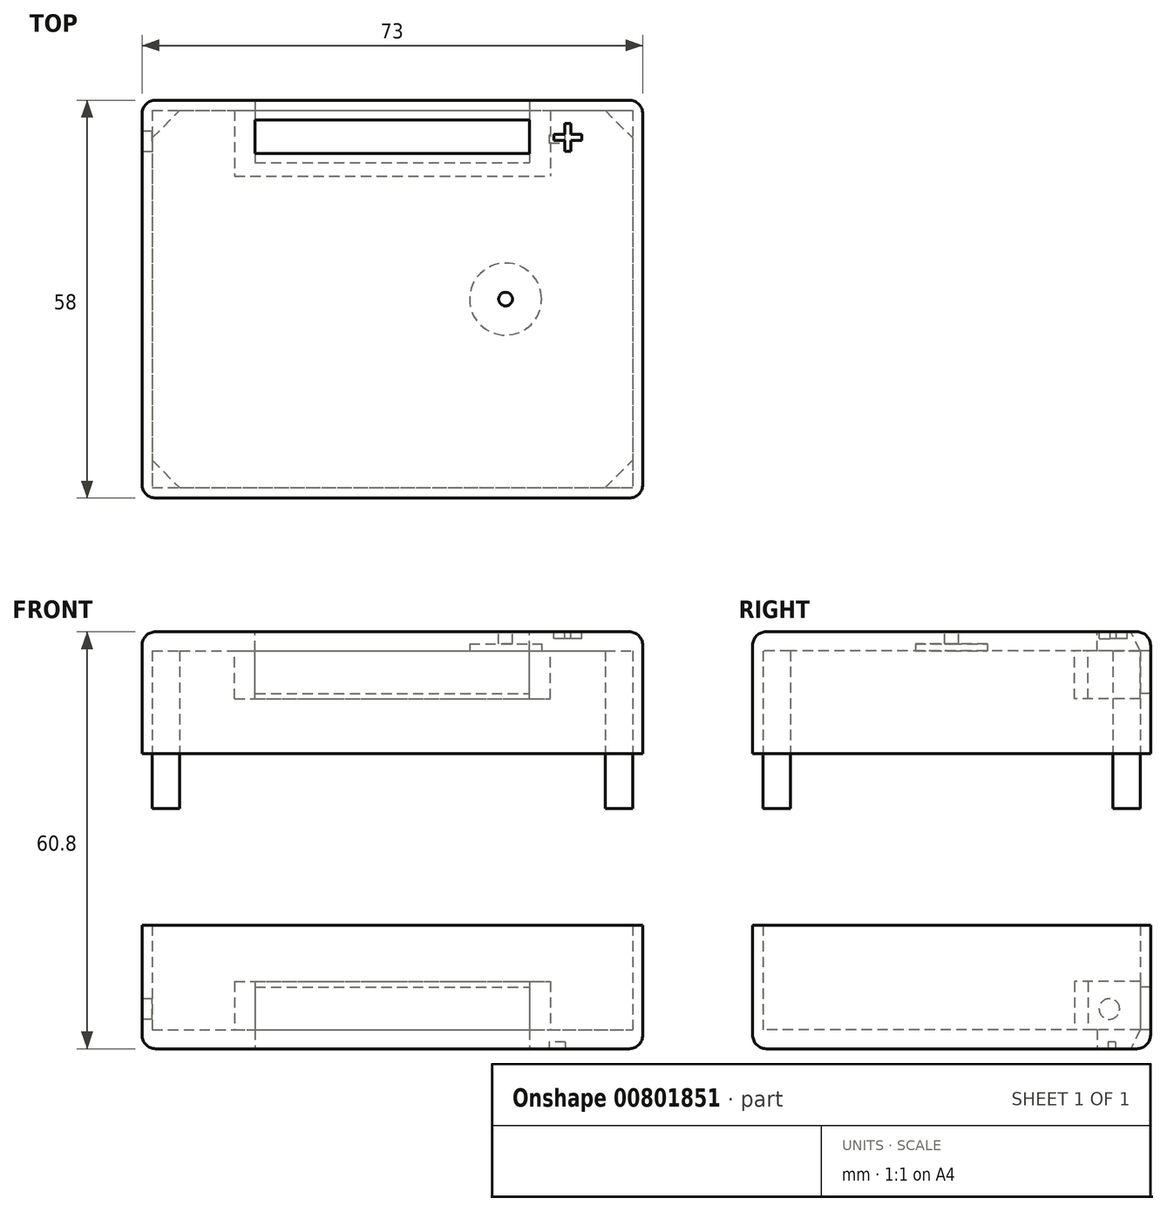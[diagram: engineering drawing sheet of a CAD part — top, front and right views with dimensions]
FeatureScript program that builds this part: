
annotation { "Feature Type Name" : "Feature", "Feature Type Description" : "" }
export const myFeature = defineFeature(function(context is Context, id is Id, definition is map)
    precondition{}
    {
        {
            var Q0;
            Q0=qCreatedBy(makeId("Top.planeOp"),FACE);
            var sketch = newSketch(context, id + "F0", { "sketchPlane" : qUnion([Q0])});
            skLineSegment(sketch, "E0.bottom", {"start": v(0, 55) * mm, "end": v(70, 55) * mm});
            skLineSegment(sketch, "E0.top", {"start": v(0, 0) * mm, "end": v(70, 0) * mm});
            skLineSegment(sketch, "E0.left", {"start": v(0, 55) * mm, "end": v(0, 0) * mm});
            skLineSegment(sketch, "E0.right", {"start": v(70, 55) * mm, "end": v(70, 0) * mm});
            skLineSegment(sketch, "E1.bottom", {"start": v(0.5, 56.5) * mm, "end": v(69.5, 56.5) * mm});
            skLineSegment(sketch, "E1.top", {"start": v(0.5, -1.5) * mm, "end": v(69.5, -1.5) * mm});
            skLineSegment(sketch, "E1.left", {"start": v(-1.5, 54.5) * mm, "end": v(-1.5, 0.5) * mm});
            skLineSegment(sketch, "E1.right", {"start": v(71.5, 54.5) * mm, "end": v(71.5, 0.5) * mm});
            skPoint(sketch, "E2.visualSharp", {"position": v(-1.5, 56.5) * mm});
            skArc(sketch, "E2.filletArc", {"start": v(0.5, 56.5) * mm, "mid": v(-0.91, 55.91) * mm, "end": v(-1.5, 54.5) * mm});
            skPoint(sketch, "E3.visualSharp", {"position": v(-1.5, -1.5) * mm});
            skArc(sketch, "E3.filletArc", {"start": v(-1.5, 0.5) * mm, "mid": v(-0.91, -0.91) * mm, "end": v(0.5, -1.5) * mm});
            skPoint(sketch, "E4.visualSharp", {"position": v(71.5, 56.5) * mm});
            skArc(sketch, "E4.filletArc", {"start": v(71.5, 54.5) * mm, "mid": v(70.91, 55.91) * mm, "end": v(69.5, 56.5) * mm});
            skPoint(sketch, "E5.visualSharp", {"position": v(71.5, -1.5) * mm});
            skArc(sketch, "E5.filletArc", {"start": v(69.5, -1.5) * mm, "mid": v(70.91, -0.91) * mm, "end": v(71.5, 0.5) * mm});
            skSolve(sketch);
        }
        {
            var Q0;
            Q0=makeQuery(id+"F0.imprint","IMPRINT",FACE,{"disambiguationData":[TD([[makeQuery(id+"F0.imprint","IMPRINT",EDGE,{"derivedFrom":sQuery(id+"F0.wireOp",EDGE,"E0.bottom")}),-1.0]])]});
            extrude(context, id + "F1", {"entities" : qUnion([Q0]), "depth" : 2.8 * mm, "offsetDistance" : 25 * mm});
        }
        {
            var Q0;
            Q0=makeQuery(id+"F0.imprint","IMPRINT",FACE,{"disambiguationData":[TD([[makeQuery(id+"F0.imprint","IMPRINT",EDGE,{"derivedFrom":sQuery(id+"F0.wireOp",EDGE,"E0.bottom")}),1.0]])]});
            extrude(context, id + "F2", {"entities" : qUnion([Q0]), "operationType" : NewBodyOperationType.ADD, "depth" : 18 * mm, "offsetDistance" : 25 * mm});
        }
        {
            var Q0;
            Q0=makeQuery(id+"F1.opExtrude","CAP_FACE",FACE,{"disambiguationData":[OSD([sQuery(id+"F0.wireOp",EDGE,"E0.bottom"),sQuery(id+"F0.wireOp",EDGE,"E0.top"),sQuery(id+"F0.wireOp",EDGE,"E0.left"),sQuery(id+"F0.wireOp",EDGE,"E0.right")])],"isStart":false});
            var sketch = newSketch(context, id + "F3", { "sketchPlane" : qUnion([Q0])});
            skLineSegment(sketch, "E6.bottom", {"start": v(12, 55) * mm, "end": v(15, 55) * mm});
            skLineSegment(sketch, "E6.right", {"start": v(15, 55) * mm, "end": v(15, 47.4) * mm});
            skLineSegment(sketch, "E7.bottom", {"start": v(55, 55) * mm, "end": v(58, 55) * mm});
            skLineSegment(sketch, "E7.left", {"start": v(55, 55) * mm, "end": v(55, 47.4) * mm});
            skLineSegment(sketch, "E8", {"start": v(12, 51.2) * mm, "end": v(0, 51.2) * mm, "construction": true});
            skLineSegment(sketch, "E9", {"start": v(58, 51.2) * mm, "end": v(70, 51.2) * mm, "construction": true});
            skLineSegment(sketch, "E10.bottom", {"start": v(15, 47.4) * mm, "end": v(55, 47.4) * mm});
            skLineSegment(sketch, "E10.top", {"start": v(12, 45.4) * mm, "end": v(58, 45.4) * mm});
            skLineSegment(sketch, "E11", {"start": v(12, 55) * mm, "end": v(12, 45.4) * mm});
            skLineSegment(sketch, "E12", {"start": v(58, 55) * mm, "end": v(58, 45.4) * mm});
            skLineSegment(sketch, "E13", {"start": v(15, 48.7) * mm, "end": v(55, 48.7) * mm});
            skLineSegment(sketch, "E14", {"start": v(15, 55) * mm, "end": v(55, 55) * mm});
            skSolve(sketch);
        }
        {
            var Q0;
            Q0=makeQuery(id+"F3.imprint","IMPRINT",FACE,{"disambiguationData":[TD([[makeQuery(id+"F3.imprint","IMPRINT",EDGE,{"derivedFrom":sQuery(id+"F3.wireOp",EDGE,"E6.bottom")}),-1.0]])]});
            var Q1;
            Q1=makeQuery(id+"F3.imprint","IMPRINT",FACE,{"disambiguationData":[TD([[makeQuery(id+"F3.imprint","IMPRINT",EDGE,{"derivedFrom":sQuery(id+"F3.wireOp",EDGE,"E7.bottom")}),-1.0]])]});
            extrude(context, id + "F4", {"entities" : qUnion([Q0, Q1]), "operationType" : NewBodyOperationType.ADD, "depth" : 7 * mm, "offsetDistance" : 25 * mm});
        }
        {
            var Q0;
            {var subQ0=sQuery(id+"F0.wireOp",EDGE,"E0.right");var subQ1=sQuery(id+"F0.wireOp",EDGE,"E0.left");var subQ2=sQuery(id+"F0.wireOp",EDGE,"E0.top");var subQ3=sQuery(id+"F0.wireOp",EDGE,"E0.bottom");Q0=makeQuery(id+"F2.boolean.opBoolean","MERGE",FACE,{"derivedFrom":[makeQuery(id+"F1.opExtrude","CAP_FACE",FACE,{"disambiguationData":[OSD([subQ3,subQ2,subQ1,subQ0])],"isStart":true}),makeQuery(id+"F2.opExtrude","CAP_FACE",FACE,{"disambiguationData":[OSD([subQ3,subQ2,subQ1,subQ0,sQuery(id+"F0.wireOp",EDGE,"E1.bottom"),sQuery(id+"F0.wireOp",EDGE,"E1.top"),sQuery(id+"F0.wireOp",EDGE,"E1.left"),sQuery(id+"F0.wireOp",EDGE,"E1.right"),sQuery(id+"F0.wireOp",EDGE,"E2.filletArc"),sQuery(id+"F0.wireOp",EDGE,"E3.filletArc"),sQuery(id+"F0.wireOp",EDGE,"E4.filletArc"),sQuery(id+"F0.wireOp",EDGE,"E5.filletArc")])],"isStart":true})]});}
            var sketch = newSketch(context, id + "F5", { "sketchPlane" : qUnion([Q0])});
            skLineSegment(sketch, "E15.0", {"start": v(15, -48.7) * mm, "end": v(55, -48.7) * mm});
            skLineSegment(sketch, "E15.1", {"start": v(15, -53.6) * mm, "end": v(15, -48.7) * mm});
            skLineSegment(sketch, "E15.2", {"start": v(55, -53.6) * mm, "end": v(55, -48.7) * mm});
            skLineSegment(sketch, "E16", {"start": v(15, -55) * mm, "end": v(55, -55) * mm, "construction": true});
            skLineSegment(sketch, "E17", {"start": v(15, -53.6) * mm, "end": v(55, -53.6) * mm});
            skSolve(sketch);
        }
        {
            var Q1;
            {var subQ2=sQuery(id+"F3.wireOp",EDGE,"E13");Q1=makeQuery(id+"F3.imprint","IMPRINT",FACE,{"disambiguationData":[TD([[makeQuery(id+"F3.imprint","IMPRINT",EDGE,{"derivedFrom":subQ2}),1.0]])]});}
            var Q2;
            Q2=makeQuery(id+"F5.imprint","IMPRINT",FACE,{"disambiguationData":[TD([[makeQuery(id+"F5.imprint","IMPRINT",EDGE,{"derivedFrom":sQuery(id+"F5.wireOp",EDGE,"E15.0")}),-1.0]])]});
            loft(context, id + "F6", {"operationType" : NewBodyOperationType.REMOVE, "sheetProfilesArray" : [{ "sheetProfileEntities" : qUnion([Q1]) }, { "sheetProfileEntities" : qUnion([Q2]) }]});
        }
        {
            var Q0;
            Q0=makeQuery(id+"F2.opExtrude","SWEPT_FACE",FACE,{"disambiguationData":[OSD([sQuery(id+"F0.wireOp",EDGE,"E0.bottom")])]});
            var sketch = newSketch(context, id + "F7", { "sketchPlane" : qUnion([Q0])});
            skLineSegment(sketch, "E18.bottom", {"start": v(15, 2.8) * mm, "end": v(55, 2.8) * mm});
            skLineSegment(sketch, "E18.top", {"start": v(15, 9) * mm, "end": v(55, 9) * mm});
            skLineSegment(sketch, "E18.left", {"start": v(15, 2.8) * mm, "end": v(15, 9) * mm});
            skLineSegment(sketch, "E18.right", {"start": v(55, 2.8) * mm, "end": v(55, 9) * mm});
            skSolve(sketch);
        }
        {
            var Q0;
            Q0=makeQuery(id+"F7.imprint","IMPRINT",FACE,{"disambiguationData":[TD([[makeQuery(id+"F7.imprint","IMPRINT",EDGE,{"derivedFrom":sQuery(id+"F7.wireOp",EDGE,"E18.bottom")}),1.0]])]});
            extrude(context, id + "F8", {"entities" : qUnion([Q0]), "operationType" : NewBodyOperationType.REMOVE, "endBound" : BoundingType.UP_TO_NEXT, "oppositeDirection" : true, "depth" : 25 * mm, "offsetDistance" : 25 * mm});
        }
        {
            var Q0;
            Q0=makeQuery(id+"F2.opExtrude","SWEPT_FACE",FACE,{"disambiguationData":[OSD([sQuery(id+"F0.wireOp",EDGE,"E1.left")])]});
            var sketch = newSketch(context, id + "F9", { "sketchPlane" : qUnion([Q0])});
            skCircle(sketch, "E19", {"center": v(-50.5, 5.8) * mm, "radius": 1.5 * mm});
            skLineSegment(sketch, "E20.0", {"start": v(-55, 2.8) * mm, "end": v(0, 2.8) * mm, "construction": true});
            skLineSegment(sketch, "E20.1", {"start": v(-55, 18) * mm, "end": v(-55, 2.8) * mm, "construction": true});
            skSolve(sketch);
        }
        {
            var Q0;
            Q0=makeQuery(id+"F9.imprint","IMPRINT",FACE,{"disambiguationData":[TD([[makeQuery(id+"F9.imprint","IMPRINT",EDGE,{"derivedFrom":sQuery(id+"F9.wireOp",EDGE,"E19")}),1.0]])]});
            extrude(context, id + "F10", {"entities" : qUnion([Q0]), "operationType" : NewBodyOperationType.REMOVE, "endBound" : BoundingType.UP_TO_NEXT, "oppositeDirection" : true, "depth" : 25 * mm, "offsetDistance" : 25 * mm});
        }
        {
            var Q0;
            Q0=makeQuery(id+"F2.opExtrude","CAP_EDGE",EDGE,{"disambiguationData":[OSD([sQuery(id+"F0.wireOp",EDGE,"E1.top")])],"isStart":true});
            fillet(context, id + "F11", {"entities" : qUnion([Q0]), "radius" : 2 * mm, "tangentPropagation" : true, "allowEdgeOverflow" : false});
        }
        {
            var Q0;
            {var subQ0=sQuery(id+"F0.wireOp",EDGE,"E0.right");var subQ1=sQuery(id+"F0.wireOp",EDGE,"E0.left");var subQ2=sQuery(id+"F0.wireOp",EDGE,"E0.top");var subQ3=sQuery(id+"F0.wireOp",EDGE,"E0.bottom");Q0=makeQuery(id+"F2.boolean.opBoolean","MERGE",FACE,{"derivedFrom":[makeQuery(id+"F1.opExtrude","CAP_FACE",FACE,{"disambiguationData":[OSD([subQ3,subQ2,subQ1,subQ0])],"isStart":true}),makeQuery(id+"F2.opExtrude","CAP_FACE",FACE,{"disambiguationData":[OSD([subQ3,subQ2,subQ1,subQ0,sQuery(id+"F0.wireOp",EDGE,"E1.bottom"),sQuery(id+"F0.wireOp",EDGE,"E1.top"),sQuery(id+"F0.wireOp",EDGE,"E1.left"),sQuery(id+"F0.wireOp",EDGE,"E1.right"),sQuery(id+"F0.wireOp",EDGE,"E2.filletArc"),sQuery(id+"F0.wireOp",EDGE,"E3.filletArc"),sQuery(id+"F0.wireOp",EDGE,"E4.filletArc"),sQuery(id+"F0.wireOp",EDGE,"E5.filletArc")])],"isStart":true})]});}
            var sketch = newSketch(context, id + "F12", { "sketchPlane" : qUnion([Q0])});
            skText(sketch, "E21", { "text": "-", "fontName": "OpenSans-Bold.ttf"});
            const initialGuessF12  = {"E21": [0.0576, -0.05323, 1, 0, 0.00644]};
            skSetInitialGuess(sketch, initialGuessF12);
            skSolve(sketch);
        }
        {
            var Q0;
            Q0=makeQuery(id+"F12.imprint","IMPRINT",FACE,{"disambiguationData":[TD([[makeQuery(id+"F12.imprint","IMPRINT",EDGE,{"derivedFrom":sQuery(id+"F12.wireOp",EDGE,"E21.sketch_text.stroke-0")}),-1.0]])]});
            extrude(context, id + "F13", {"entities" : qUnion([Q0]), "operationType" : NewBodyOperationType.REMOVE, "oppositeDirection" : true, "depth" : 1 * mm, "offsetDistance" : 25 * mm});
        }
        {
            var Q0;
            Q0=makeQuery(id+"F2.opExtrude","CAP_FACE",FACE,{"disambiguationData":[OSD([sQuery(id+"F0.wireOp",EDGE,"E0.bottom"),sQuery(id+"F0.wireOp",EDGE,"E0.top"),sQuery(id+"F0.wireOp",EDGE,"E0.left"),sQuery(id+"F0.wireOp",EDGE,"E0.right"),sQuery(id+"F0.wireOp",EDGE,"E1.bottom"),sQuery(id+"F0.wireOp",EDGE,"E1.top"),sQuery(id+"F0.wireOp",EDGE,"E1.left"),sQuery(id+"F0.wireOp",EDGE,"E1.right"),sQuery(id+"F0.wireOp",EDGE,"E2.filletArc"),sQuery(id+"F0.wireOp",EDGE,"E3.filletArc"),sQuery(id+"F0.wireOp",EDGE,"E4.filletArc"),sQuery(id+"F0.wireOp",EDGE,"E5.filletArc")])],"isStart":false});
            cPlane(context, id + "F14", {"entities" : qUnion([Q0]), "cplaneType" : CPlaneType.OFFSET, "offset" : 25 * mm, "width" : 150 * mm, "height" : 150 * mm});
        }
        {
            var Q0;
            Q0=qCreatedBy(id+"F14.planeOp",FACE);
            var sketch = newSketch(context, id + "F15", { "sketchPlane" : qUnion([Q0])});
            skLineSegment(sketch, "E22.0", {"start": v(0, 55) * mm, "end": v(70, 55) * mm});
            skLineSegment(sketch, "E22.1", {"start": v(0, 55) * mm, "end": v(0, 0) * mm});
            skLineSegment(sketch, "E22.2", {"start": v(0, 0) * mm, "end": v(70, 0) * mm});
            skLineSegment(sketch, "E22.3", {"start": v(70, 55) * mm, "end": v(70, 0) * mm});
            skLineSegment(sketch, "E22.4", {"start": v(0.5, 56.5) * mm, "end": v(69.5, 56.5) * mm});
            skArc(sketch, "E22.5", {"start": v(0.5, 56.5) * mm, "mid": v(-0.91, 55.91) * mm, "end": v(-1.5, 54.5) * mm});
            skLineSegment(sketch, "E22.6", {"start": v(-1.5, 54.5) * mm, "end": v(-1.5, 0.5) * mm});
            skArc(sketch, "E22.7", {"start": v(-1.5, 0.5) * mm, "mid": v(-0.91, -0.91) * mm, "end": v(0.5, -1.5) * mm});
            skLineSegment(sketch, "E22.8", {"start": v(0.5, -1.5) * mm, "end": v(69.5, -1.5) * mm});
            skArc(sketch, "E22.9", {"start": v(69.5, -1.5) * mm, "mid": v(70.91, -0.91) * mm, "end": v(71.5, 0.5) * mm});
            skLineSegment(sketch, "E22.10", {"start": v(71.5, 54.5) * mm, "end": v(71.5, 0.5) * mm});
            skArc(sketch, "E22.11", {"start": v(71.5, 54.5) * mm, "mid": v(70.91, 55.91) * mm, "end": v(69.5, 56.5) * mm});
            skLineSegment(sketch, "E23", {"start": v(0, 51) * mm, "end": v(4, 55) * mm});
            skLineSegment(sketch, "E24", {"start": v(66, 55) * mm, "end": v(70, 51) * mm});
            skLineSegment(sketch, "E25", {"start": v(66, 0) * mm, "end": v(70, 4) * mm});
            skLineSegment(sketch, "E26", {"start": v(0, 4) * mm, "end": v(4, 0) * mm});
            skSolve(sketch);
        }
        {
            var Q0;
            Q0=makeQuery(id+"F15.imprint","IMPRINT",FACE,{"disambiguationData":[TD([[makeQuery(id+"F15.imprint","IMPRINT",EDGE,{"derivedFrom":sQuery(id+"F15.wireOp",EDGE,"E22.4")}),-1.0]])]});
            var Q1;
            {var subQ3=sQuery(id+"F15.wireOp",EDGE,"E26");Q1=makeQuery(id+"F15.imprint","IMPRINT",FACE,{"disambiguationData":[TD([[makeQuery(id+"F15.imprint","IMPRINT",EDGE,{"derivedFrom":subQ3}),-1.0]])]});}
            var Q2;
            {var subQ3=sQuery(id+"F15.wireOp",EDGE,"E23");Q2=makeQuery(id+"F15.imprint","IMPRINT",FACE,{"disambiguationData":[TD([[makeQuery(id+"F15.imprint","IMPRINT",EDGE,{"derivedFrom":subQ3}),1.0]])]});}
            var Q3;
            {var subQ3=sQuery(id+"F15.wireOp",EDGE,"E24");Q3=makeQuery(id+"F15.imprint","IMPRINT",FACE,{"disambiguationData":[TD([[makeQuery(id+"F15.imprint","IMPRINT",EDGE,{"derivedFrom":subQ3}),1.0]])]});}
            var Q4;
            {var subQ3=sQuery(id+"F15.wireOp",EDGE,"E25");Q4=makeQuery(id+"F15.imprint","IMPRINT",FACE,{"disambiguationData":[TD([[makeQuery(id+"F15.imprint","IMPRINT",EDGE,{"derivedFrom":subQ3}),-1.0]])]});}
            extrude(context, id + "F16", {"entities" : qUnion([Q0, Q1, Q2, Q3, Q4]), "depth" : 15 * mm, "offsetDistance" : 25 * mm});
        }
        {
            var Q0;
            Q0=makeQuery(id+"F16.opExtrude","CAP_FACE",FACE,{"disambiguationData":[OSD([sQuery(id+"F15.wireOp",EDGE,"E22.0"),sQuery(id+"F15.wireOp",EDGE,"E22.1"),sQuery(id+"F15.wireOp",EDGE,"E22.2"),sQuery(id+"F15.wireOp",EDGE,"E22.3"),sQuery(id+"F15.wireOp",EDGE,"E22.4"),sQuery(id+"F15.wireOp",EDGE,"E22.5"),sQuery(id+"F15.wireOp",EDGE,"E22.6"),sQuery(id+"F15.wireOp",EDGE,"E22.7"),sQuery(id+"F15.wireOp",EDGE,"E22.8"),sQuery(id+"F15.wireOp",EDGE,"E22.9"),sQuery(id+"F15.wireOp",EDGE,"E22.10"),sQuery(id+"F15.wireOp",EDGE,"E22.11")])],"isStart":false});
            var sketch = newSketch(context, id + "F17", { "sketchPlane" : qUnion([Q0])});
            skArc(sketch, "E27.0", {"start": v(0.5, 56.5) * mm, "mid": v(-0.91, 55.91) * mm, "end": v(-1.5, 54.5) * mm});
            skLineSegment(sketch, "E27.1", {"start": v(-1.5, 54.5) * mm, "end": v(-1.5, 0.5) * mm});
            skArc(sketch, "E27.2", {"start": v(-1.5, 0.5) * mm, "mid": v(-0.91, -0.91) * mm, "end": v(0.5, -1.5) * mm});
            skLineSegment(sketch, "E27.3", {"start": v(0.5, -1.5) * mm, "end": v(69.5, -1.5) * mm});
            skArc(sketch, "E27.4", {"start": v(69.5, -1.5) * mm, "mid": v(70.91, -0.91) * mm, "end": v(71.5, 0.5) * mm});
            skLineSegment(sketch, "E27.5", {"start": v(71.5, 54.5) * mm, "end": v(71.5, 0.5) * mm});
            skArc(sketch, "E27.6", {"start": v(71.5, 54.5) * mm, "mid": v(70.91, 55.91) * mm, "end": v(69.5, 56.5) * mm});
            skLineSegment(sketch, "E27.7", {"start": v(0.5, 56.5) * mm, "end": v(69.5, 56.5) * mm});
            skSolve(sketch);
        }
        {
            var Q0;
            Q0=makeQuery(id+"F17.imprint","IMPRINT",FACE,{"disambiguationData":[TD([[makeQuery(id+"F17.imprint","IMPRINT",EDGE,{"derivedFrom":makeQuery(id+"F16.opExtrude","CAP_EDGE",EDGE,{"disambiguationData":[OSD([sQuery(id+"F15.wireOp",EDGE,"E22.0")])],"isStart":false})}),-1.0]])]});
            var Q1;
            Q1=makeQuery(id+"F17.imprint","IMPRINT",FACE,{"disambiguationData":[TD([[makeQuery(id+"F17.imprint","IMPRINT",EDGE,{"derivedFrom":sQuery(id+"F17.wireOp",EDGE,"E27.0")}),1.0]])]});
            extrude(context, id + "F18", {"entities" : qUnion([Q0, Q1]), "operationType" : NewBodyOperationType.ADD, "depth" : 2.8 * mm, "offsetDistance" : 25 * mm});
        }
        {
            var Q0;
            Q0=makeQuery(id+"F18.opExtrude","CAP_FACE",FACE,{"disambiguationData":[OSD([sQuery(id+"F17.wireOp",EDGE,"E27.0"),sQuery(id+"F17.wireOp",EDGE,"E27.1"),sQuery(id+"F17.wireOp",EDGE,"E27.2"),sQuery(id+"F17.wireOp",EDGE,"E27.3"),sQuery(id+"F17.wireOp",EDGE,"E27.4"),sQuery(id+"F17.wireOp",EDGE,"E27.5"),sQuery(id+"F17.wireOp",EDGE,"E27.6"),sQuery(id+"F17.wireOp",EDGE,"E27.7")])],"isStart":true});
            var sketch = newSketch(context, id + "F19", { "sketchPlane" : qUnion([Q0])});
            skLineSegment(sketch, "E28.0", {"start": v(12, -55) * mm, "end": v(15, -55) * mm});
            skLineSegment(sketch, "E28.1", {"start": v(15, -55) * mm, "end": v(15, -47.4) * mm});
            skLineSegment(sketch, "E28.2", {"start": v(55, -55) * mm, "end": v(58, -55) * mm});
            skLineSegment(sketch, "E28.3", {"start": v(55, -55) * mm, "end": v(55, -47.4) * mm});
            skLineSegment(sketch, "E28.4", {"start": v(12, -51.2) * mm, "end": v(0, -51.2) * mm, "construction": true});
            skLineSegment(sketch, "E28.5", {"start": v(58, -51.2) * mm, "end": v(70, -51.2) * mm, "construction": true});
            skLineSegment(sketch, "E28.6", {"start": v(15, -47.4) * mm, "end": v(55, -47.4) * mm});
            skLineSegment(sketch, "E28.7", {"start": v(12, -45.4) * mm, "end": v(58, -45.4) * mm});
            skLineSegment(sketch, "E28.8", {"start": v(12, -55) * mm, "end": v(12, -45.4) * mm});
            skLineSegment(sketch, "E28.9", {"start": v(58, -55) * mm, "end": v(58, -45.4) * mm});
            skLineSegment(sketch, "E28.10", {"start": v(15, -48.7) * mm, "end": v(55, -48.7) * mm});
            skLineSegment(sketch, "E28.11", {"start": v(15, -55) * mm, "end": v(55, -55) * mm});
            skSolve(sketch);
        }
        {
            var Q0;
            Q0=makeQuery(id+"F18.opExtrude","CAP_FACE",FACE,{"disambiguationData":[OSD([sQuery(id+"F17.wireOp",EDGE,"E27.0"),sQuery(id+"F17.wireOp",EDGE,"E27.1"),sQuery(id+"F17.wireOp",EDGE,"E27.2"),sQuery(id+"F17.wireOp",EDGE,"E27.3"),sQuery(id+"F17.wireOp",EDGE,"E27.4"),sQuery(id+"F17.wireOp",EDGE,"E27.5"),sQuery(id+"F17.wireOp",EDGE,"E27.6"),sQuery(id+"F17.wireOp",EDGE,"E27.7")])],"isStart":false});
            var sketch = newSketch(context, id + "F20", { "sketchPlane" : qUnion([Q0])});
            skLineSegment(sketch, "E29.0.0", {"start": v(15, 48.7) * mm, "end": v(15, 53.6) * mm});
            skLineSegment(sketch, "E29.0.1", {"start": v(15, 53.6) * mm, "end": v(55, 53.6) * mm});
            skLineSegment(sketch, "E29.0.2", {"start": v(55, 53.6) * mm, "end": v(55, 48.7) * mm});
            skLineSegment(sketch, "E29.0.3", {"start": v(55, 48.7) * mm, "end": v(15, 48.7) * mm});
            skSolve(sketch);
        }
        {
            var Q1;
            {var subQ2=sQuery(id+"F19.wireOp",EDGE,"E28.10");Q1=makeQuery(id+"F19.imprint","IMPRINT",FACE,{"disambiguationData":[TD([[makeQuery(id+"F19.imprint","IMPRINT",EDGE,{"derivedFrom":subQ2}),-1.0]])]});}
            var Q2;
            Q2=makeQuery(id+"F20.imprint","IMPRINT",FACE,{"disambiguationData":[TD([[makeQuery(id+"F20.imprint","IMPRINT",EDGE,{"derivedFrom":sQuery(id+"F20.wireOp",EDGE,"E29.0.0")}),-1.0]])]});
            loft(context, id + "F21", {"operationType" : NewBodyOperationType.REMOVE, "sheetProfilesArray" : [{ "sheetProfileEntities" : qUnion([Q1]) }, { "sheetProfileEntities" : qUnion([Q2]) }]});
        }
        {
            var Q0;
            {var subQ6=sQuery(id+"F19.wireOp",EDGE,"E28.0");Q0=makeQuery(id+"F19.imprint","IMPRINT",FACE,{"disambiguationData":[TD([[makeQuery(id+"F19.imprint","IMPRINT",EDGE,{"derivedFrom":subQ6}),1.0]])]});}
            extrude(context, id + "F22", {"entities" : qUnion([Q0]), "operationType" : NewBodyOperationType.ADD, "depth" : 7 * mm, "offsetDistance" : 25 * mm});
        }
        {
            var Q0;
            Q0=makeQuery(id+"F16.opExtrude","SWEPT_FACE",FACE,{"disambiguationData":[OSD([sQuery(id+"F15.wireOp",EDGE,"E22.0")])]});
            var sketch = newSketch(context, id + "F23", { "sketchPlane" : qUnion([Q0])});
            skLineSegment(sketch, "E30.bottom", {"start": v(15, 58) * mm, "end": v(55, 58) * mm});
            skLineSegment(sketch, "E30.top", {"start": v(15, 51.8) * mm, "end": v(55, 51.8) * mm});
            skLineSegment(sketch, "E30.left", {"start": v(15, 58) * mm, "end": v(15, 51.8) * mm});
            skLineSegment(sketch, "E30.right", {"start": v(55, 58) * mm, "end": v(55, 51.8) * mm});
            skSolve(sketch);
        }
        {
            var Q0;
            Q0=makeQuery(id+"F23.imprint","IMPRINT",FACE,{"disambiguationData":[TD([[makeQuery(id+"F23.imprint","IMPRINT",EDGE,{"derivedFrom":sQuery(id+"F23.wireOp",EDGE,"E30.bottom")}),1.0]])]});
            extrude(context, id + "F24", {"entities" : qUnion([Q0]), "operationType" : NewBodyOperationType.REMOVE, "endBound" : BoundingType.UP_TO_NEXT, "oppositeDirection" : true, "depth" : 25 * mm, "offsetDistance" : 25 * mm});
        }
        {
            var Q0;
            Q0=makeQuery(id+"F18.opExtrude","CAP_FACE",FACE,{"disambiguationData":[OSD([sQuery(id+"F17.wireOp",EDGE,"E27.0"),sQuery(id+"F17.wireOp",EDGE,"E27.1"),sQuery(id+"F17.wireOp",EDGE,"E27.2"),sQuery(id+"F17.wireOp",EDGE,"E27.3"),sQuery(id+"F17.wireOp",EDGE,"E27.4"),sQuery(id+"F17.wireOp",EDGE,"E27.5"),sQuery(id+"F17.wireOp",EDGE,"E27.6"),sQuery(id+"F17.wireOp",EDGE,"E27.7")])],"isStart":false});
            var sketch = newSketch(context, id + "F25", { "sketchPlane" : qUnion([Q0])});
            skText(sketch, "E31", { "text": "+", "fontName": "OpenSans-Bold.ttf"});
            const initialGuessF25  = {"E31": [0.05818, 0.04814, 1, 0, 0.006]};
            skSetInitialGuess(sketch, initialGuessF25);
            skSolve(sketch);
        }
        {
            var Q0;
            Q0=makeQuery(id+"F25.imprint","IMPRINT",FACE,{"disambiguationData":[TD([[makeQuery(id+"F25.imprint","IMPRINT",EDGE,{"derivedFrom":sQuery(id+"F25.wireOp",EDGE,"E31.sketch_text.stroke-0")}),-1.0]])]});
            extrude(context, id + "F26", {"entities" : qUnion([Q0]), "operationType" : NewBodyOperationType.REMOVE, "oppositeDirection" : true, "depth" : 1 * mm, "offsetDistance" : 25 * mm});
        }
        {
            var Q0;
            Q0=makeQuery(id+"F18.opExtrude","CAP_EDGE",EDGE,{"disambiguationData":[OSD([sQuery(id+"F17.wireOp",EDGE,"E27.3")])],"isStart":false});
            fillet(context, id + "F27", {"entities" : qUnion([Q0]), "radius" : 2 * mm, "tangentPropagation" : true, "allowEdgeOverflow" : false});
        }
        {
            var Q0;
            Q0=makeQuery(id+"F18.opExtrude","CAP_FACE",FACE,{"disambiguationData":[OSD([sQuery(id+"F17.wireOp",EDGE,"E27.0"),sQuery(id+"F17.wireOp",EDGE,"E27.1"),sQuery(id+"F17.wireOp",EDGE,"E27.2"),sQuery(id+"F17.wireOp",EDGE,"E27.3"),sQuery(id+"F17.wireOp",EDGE,"E27.4"),sQuery(id+"F17.wireOp",EDGE,"E27.5"),sQuery(id+"F17.wireOp",EDGE,"E27.6"),sQuery(id+"F17.wireOp",EDGE,"E27.7")])],"isStart":false});
            var sketch = newSketch(context, id + "F28", { "sketchPlane" : qUnion([Q0])});
            skCircle(sketch, "E32", {"center": v(51.5, 27.5) * mm, "radius": 1 * mm});
            skLineSegment(sketch, "E33", {"start": v(51.5, 54.5) * mm, "end": v(51.5, 0.5) * mm, "construction": true});
            skSolve(sketch);
        }
        {
            var Q0;
            Q0=makeQuery(id+"F28.imprint","IMPRINT",FACE,{"disambiguationData":[TD([[makeQuery(id+"F28.imprint","IMPRINT",EDGE,{"derivedFrom":sQuery(id+"F28.wireOp",EDGE,"E32")}),1.0]])]});
            extrude(context, id + "F29", {"entities" : qUnion([Q0]), "operationType" : NewBodyOperationType.REMOVE, "endBound" : BoundingType.UP_TO_NEXT, "oppositeDirection" : true, "depth" : 25 * mm, "offsetDistance" : 25 * mm});
        }
        {
            var Q0;
            Q0=makeQuery(id+"F22.boolean.opBoolean","SPLIT",FACE,{"disambiguationData":[TD([makeQuery(id+"F16.opExtrude","SWEPT_FACE",FACE,{"disambiguationData":[OSD([sQuery(id+"F15.wireOp",EDGE,"E22.0")])]})])],"derivedFrom":makeQuery(id+"F18.opExtrude","CAP_FACE",FACE,{"disambiguationData":[OSD([sQuery(id+"F17.wireOp",EDGE,"E27.0"),sQuery(id+"F17.wireOp",EDGE,"E27.1"),sQuery(id+"F17.wireOp",EDGE,"E27.2"),sQuery(id+"F17.wireOp",EDGE,"E27.3"),sQuery(id+"F17.wireOp",EDGE,"E27.4"),sQuery(id+"F17.wireOp",EDGE,"E27.5"),sQuery(id+"F17.wireOp",EDGE,"E27.6"),sQuery(id+"F17.wireOp",EDGE,"E27.7")])],"isStart":true})});
            var sketch = newSketch(context, id + "F30", { "sketchPlane" : qUnion([Q0])});
            skCircle(sketch, "E34", {"center": v(51.5, -27.5) * mm, "radius": 5.25 * mm});
            skSolve(sketch);
        }
        {
            var Q0;
            Q0=makeQuery(id+"F30.imprint","IMPRINT",FACE,{"disambiguationData":[TD([[makeQuery(id+"F30.imprint","IMPRINT",EDGE,{"derivedFrom":sQuery(id+"F30.wireOp",EDGE,"E34")}),1.0]])]});
            extrude(context, id + "F31", {"entities" : qUnion([Q0]), "operationType" : NewBodyOperationType.REMOVE, "oppositeDirection" : true, "depth" : 1 * mm, "offsetDistance" : 25 * mm});
        }
        {
            var Q0;
            {var subQ3=sQuery(id+"F15.wireOp",EDGE,"E26");Q0=makeQuery(id+"F15.imprint","IMPRINT",FACE,{"disambiguationData":[TD([[makeQuery(id+"F15.imprint","IMPRINT",EDGE,{"derivedFrom":subQ3}),-1.0]])]});}
            var Q1;
            {var subQ3=sQuery(id+"F15.wireOp",EDGE,"E25");Q1=makeQuery(id+"F15.imprint","IMPRINT",FACE,{"disambiguationData":[TD([[makeQuery(id+"F15.imprint","IMPRINT",EDGE,{"derivedFrom":subQ3}),-1.0]])]});}
            var Q2;
            {var subQ3=sQuery(id+"F15.wireOp",EDGE,"E24");Q2=makeQuery(id+"F15.imprint","IMPRINT",FACE,{"disambiguationData":[TD([[makeQuery(id+"F15.imprint","IMPRINT",EDGE,{"derivedFrom":subQ3}),1.0]])]});}
            var Q3;
            {var subQ3=sQuery(id+"F15.wireOp",EDGE,"E23");Q3=makeQuery(id+"F15.imprint","IMPRINT",FACE,{"disambiguationData":[TD([[makeQuery(id+"F15.imprint","IMPRINT",EDGE,{"derivedFrom":subQ3}),1.0]])]});}
            extrude(context, id + "F32", {"entities" : qUnion([Q0, Q1, Q2, Q3]), "operationType" : NewBodyOperationType.ADD, "oppositeDirection" : true, "depth" : 8 * mm, "offsetDistance" : 25 * mm});
        }
    });
